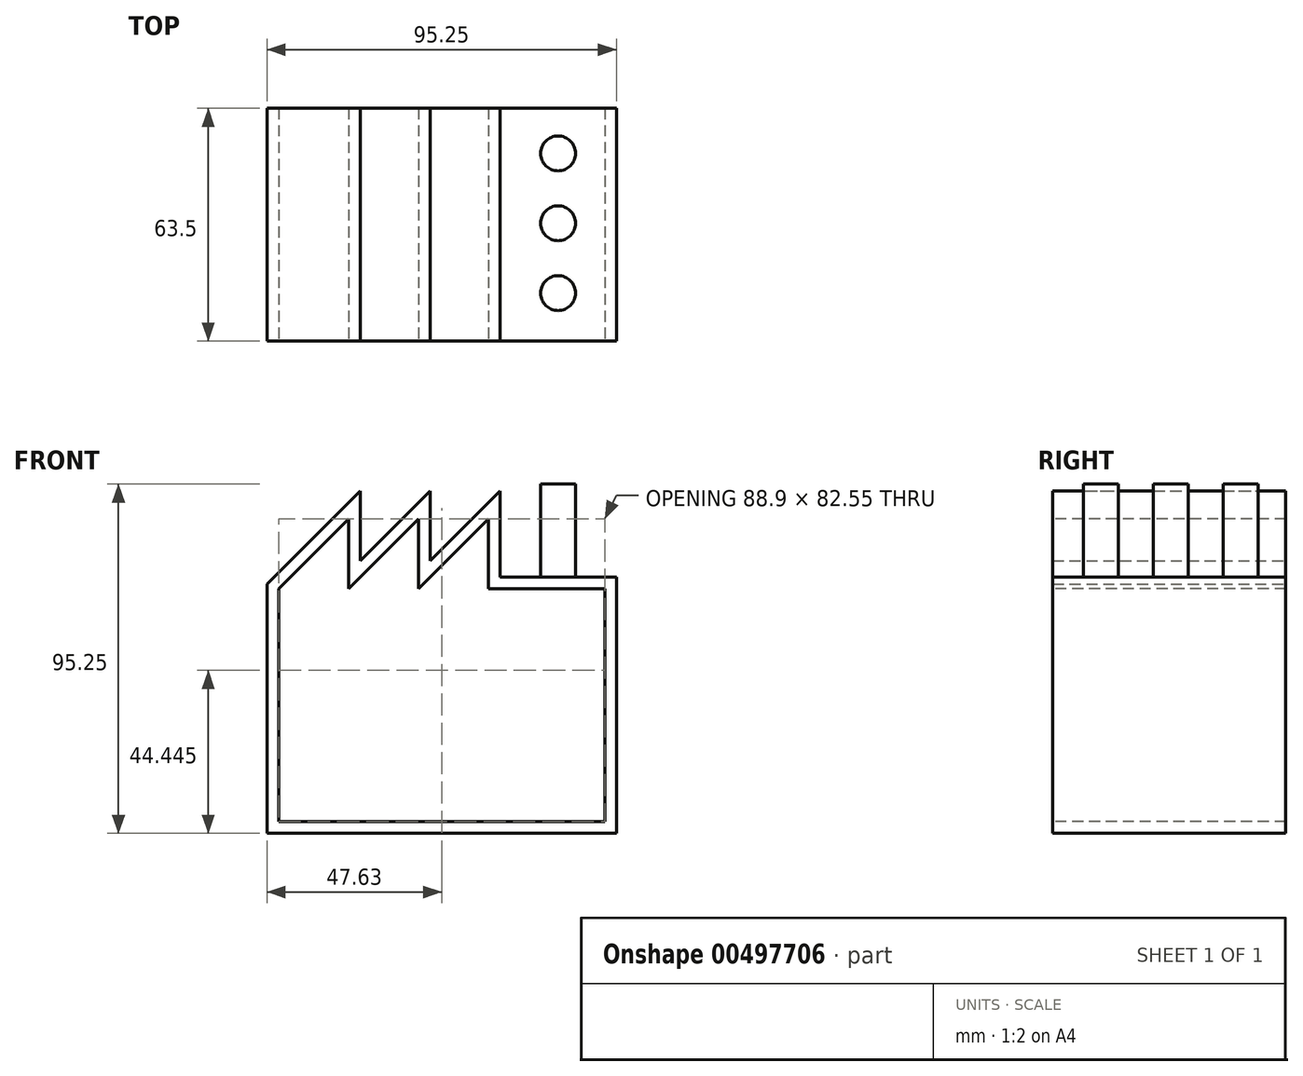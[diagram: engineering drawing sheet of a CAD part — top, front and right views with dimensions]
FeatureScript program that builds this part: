
annotation { "Feature Type Name" : "Feature", "Feature Type Description" : "" }
export const myFeature = defineFeature(function(context is Context, id is Id, definition is map)
    precondition{}
    {
        {
            var Q0;
            Q0=qCreatedBy(makeId("Front.planeOp"),FACE);
            var sketch = newSketch(context, id + "F0", { "sketchPlane" : qUnion([Q0])});
            skLineSegment(sketch, "E0.bottom", {"start": v(44.45, -31.75) * mm, "end": v(-44.45, -31.75) * mm});
            skLineSegment(sketch, "E0.top", {"start": v(44.45, 31.75) * mm, "end": v(12.7, 31.75) * mm});
            skLineSegment(sketch, "E0.left", {"start": v(44.45, -31.75) * mm, "end": v(44.45, 31.75) * mm});
            skLineSegment(sketch, "E0.right", {"start": v(-44.45, -31.75) * mm, "end": v(-44.45, 31.75) * mm});
            skPoint(sketch, "E0.middle", {"position": v(0, 0) * mm});
            skLineSegment(sketch, "E1.right", {"start": v(-25.4, 31.75) * mm, "end": v(-25.4, 50.8) * mm});
            skLineSegment(sketch, "E2", {"start": v(-44.45, 31.75) * mm, "end": v(-25.4, 50.8) * mm});
            skLineSegment(sketch, "E3.1.0.0", {"start": v(-6.35, 31.75) * mm, "end": v(-6.35, 50.8) * mm});
            skLineSegment(sketch, "E3.1.0.1", {"start": v(-25.4, 31.75) * mm, "end": v(-6.35, 50.8) * mm});
            skLineSegment(sketch, "E3.2.0.0", {"start": v(12.7, 31.75) * mm, "end": v(12.7, 50.8) * mm});
            skLineSegment(sketch, "E3.2.0.1", {"start": v(-6.35, 31.75) * mm, "end": v(12.7, 50.8) * mm});
            skSolve(sketch);
        }
        {
            var Q0;
            Q0=qCreatedBy(makeId("Front.planeOp"),FACE);
            var sketch = newSketch(context, id + "F1", { "sketchPlane" : qUnion([Q0])});
            skLineSegment(sketch, "E4.0", {"start": v(15.88, 34.93) * mm, "end": v(15.87, 58.47) * mm});
            skLineSegment(sketch, "E4.1", {"start": v(47.62, 34.93) * mm, "end": v(15.88, 34.93) * mm});
            skLineSegment(sketch, "E4.2", {"start": v(15.87, 58.47) * mm, "end": v(-3.18, 39.42) * mm});
            skLineSegment(sketch, "E4.3", {"start": v(47.63, -34.92) * mm, "end": v(47.62, 34.93) * mm});
            skLineSegment(sketch, "E4.4", {"start": v(-47.62, -34.93) * mm, "end": v(47.63, -34.92) * mm});
            skLineSegment(sketch, "E4.5", {"start": v(-47.63, 33.07) * mm, "end": v(-47.62, -34.93) * mm});
            skLineSegment(sketch, "E4.6", {"start": v(-3.17, 39.42) * mm, "end": v(-3.18, 58.47) * mm});
            skLineSegment(sketch, "E4.7", {"start": v(-3.17, 58.47) * mm, "end": v(-22.22, 39.42) * mm});
            skLineSegment(sketch, "E4.8", {"start": v(-22.22, 39.42) * mm, "end": v(-22.22, 58.47) * mm});
            skLineSegment(sketch, "E4.9", {"start": v(-22.22, 58.47) * mm, "end": v(-47.63, 33.07) * mm});
            skSolve(sketch);
        }
        {
            var Q0;
            Q0 = qSketchRegion(id + "F1", true);
            extrude(context, id + "F2", {"entities" : qUnion([Q0]), "depth" : 31.75 * mm, "offsetDistance" : 25.4 * mm, "hasSecondDirection" : true, "secondDirectionOppositeDirection" : true, "secondDirectionDepth" : 31.75 * mm});
        }
        {
            var Q0;
            Q0 = qSketchRegion(id + "F0", true);
            extrude(context, id + "F3", {"entities" : qUnion([Q0]), "operationType" : NewBodyOperationType.REMOVE, "oppositeDirection" : true, "depth" : 64.52 * mm, "offsetDistance" : 25.4 * mm, "hasSecondDirection" : true, "secondDirectionOppositeDirection" : false, "secondDirectionDepth" : 80.52 * mm});
        }
        {
            var Q0;
            Q0=makeQuery(id+"F2.opExtrude","SWEPT_FACE",FACE,{"disambiguationData":[OSD([sQuery(id+"F1.wireOp",EDGE,"E4.1")])]});
            var sketch = newSketch(context, id + "F4", { "sketchPlane" : qUnion([Q0])});
            skCircle(sketch, "E5", {"center": v(31.75, 19.46) * mm, "radius": 4.76 * mm});
            skCircle(sketch, "E6.0.1.0", {"center": v(31.75, 0.41) * mm, "radius": 4.76 * mm});
            skCircle(sketch, "E6.0.2.0", {"center": v(31.75, -18.64) * mm, "radius": 4.76 * mm});
            skLineSegment(sketch, "E6.direction1", {"start": v(31.75, 19.46) * mm, "end": v(57.15, 19.46) * mm, "construction": true});
            skLineSegment(sketch, "E6.direction2", {"start": v(31.75, 19.46) * mm, "end": v(31.75, 0.41) * mm, "construction": true});
            skSolve(sketch);
        }
        {
            var Q0;
            Q0 = qSketchRegion(id + "F4", true);
            extrude(context, id + "F5", {"entities" : qUnion([Q0]), "operationType" : NewBodyOperationType.ADD, "depth" : 25.4 * mm, "offsetDistance" : 25.4 * mm});
        }
    });
